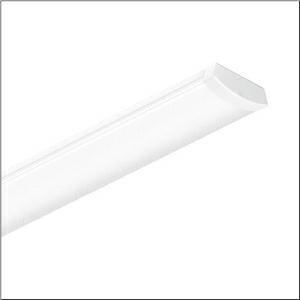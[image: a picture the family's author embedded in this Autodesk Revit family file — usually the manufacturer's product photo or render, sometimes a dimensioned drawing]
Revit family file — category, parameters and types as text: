
# Revit family: siluette_r__21_51ln12mnm70a_66ce
name_source: partatom
category: Lighting Fixtures
units: mm (PartAtom-declared; Revit-internal decimal feet)

## family parameters
Cut with Voids When Loaded = No
Host = Face
Light Source = No
Part Type = Normal
Room Calculation Point = No
Round Connector Dimension = Use Diameter
Shared = No

## types (1)
- --- (1 x LED, 4320 lm, 28.8 W, 5000K)
    Apparent Load = 29 VA
    CIE Flux Codes = 43 73 92 94 100
    Color Rendering = 80
    Color Temperature = 5000K
    Default Elevation = 1800 mm
    Description = Siluette® 21, office luminaire, primary optical cover: enclosure, of PC, frosted, light emission: direct distribution, primary light characteristic: symmetric, installation type: suspended mounting, surface-mounted, LED, rated luminous flux: 7.150lm, luminous efficacy: 147lm/W, light colour: 830/840/850, colour temperature: 3000/4000/5000K, control gear: ON/OFF Multilumen, with terminal, 3-pole, mains connection: 220..240V, AC, 50/60Hz, rated input power: 49W, housing, of sheet steel, white, length: 1.500mm, width: 152mm, height: 53mm, end cap, of PMMA, white, protection rating (complete): IP44, insulation class (complete): insulation class I (protective earthing), certification: CE, UKCA, protection symbol: D, impact resistance: IK04, permissible operating ambient temperature: -20..+40°C, contact your sales advisor before using the luminaires in applications with unclear chemical exposure, large temperature fluctuations or condensation-forming humidity, corresponds to IFS (International Featured Standards) requirements for safety and quality in the food industry, packaging unit: 1 piece
    Height = 52 mm  [stored 0.170604 ft]
    Lamp = 1 x LED
    Lamp Light Flux = 4320 lm
    Lamp Power = 28.8 W
    Lamp count = 1
    Length = 1485 mm
    Luminous efficacy = 150 lm/W
    Manufacturer = Siteco
    ModVariant = No
    Model = 51LN12MNM70A
    Mounting Place = Ceiling
    Mounting Type = Pendant
    Number of Poles = 1
    OnlyDefault = Yes
    Power Factor = 1
    Product Name = Siluette® 21
    Product group = office luminaire | ceiling pendant
    ProductGroupID = 904
    Protection Class = Protection class I
    Protection Degree = IP 44
    RLX_Detail_Level = 1
    RLX_Emergency_Light_Flux = 0 lm
    RLX_Emergency_Type = 0
    RLX_Emergency_Type_DB = No
    RlxData = <blob elided: 19221 chars, md5=70f5039c>
    Socket = socket
    Standby Power = 0 W
    System Light Flux = 4320 lm
    System Power = 29 W
    Type Comments = individual setting: colour temperature 5000K, luminous flux: 61 % | (OFF | OFF | ON) | 200 mA
    Type Image = l_1296910.jpg
    URL = http://relux.com
    VarID = @adj_059376
    Voltage = 0 V
    Weight = 0.00 kg
    Width = 152 mm

note: [stored X ft] marks values corroborated as IEEE doubles in the binary element streams (Revit-internal decimal feet)

## geometry (parser evidence)
native form markers: Blend x4, Sweep x12
no freeform markers — native parametric forms only
